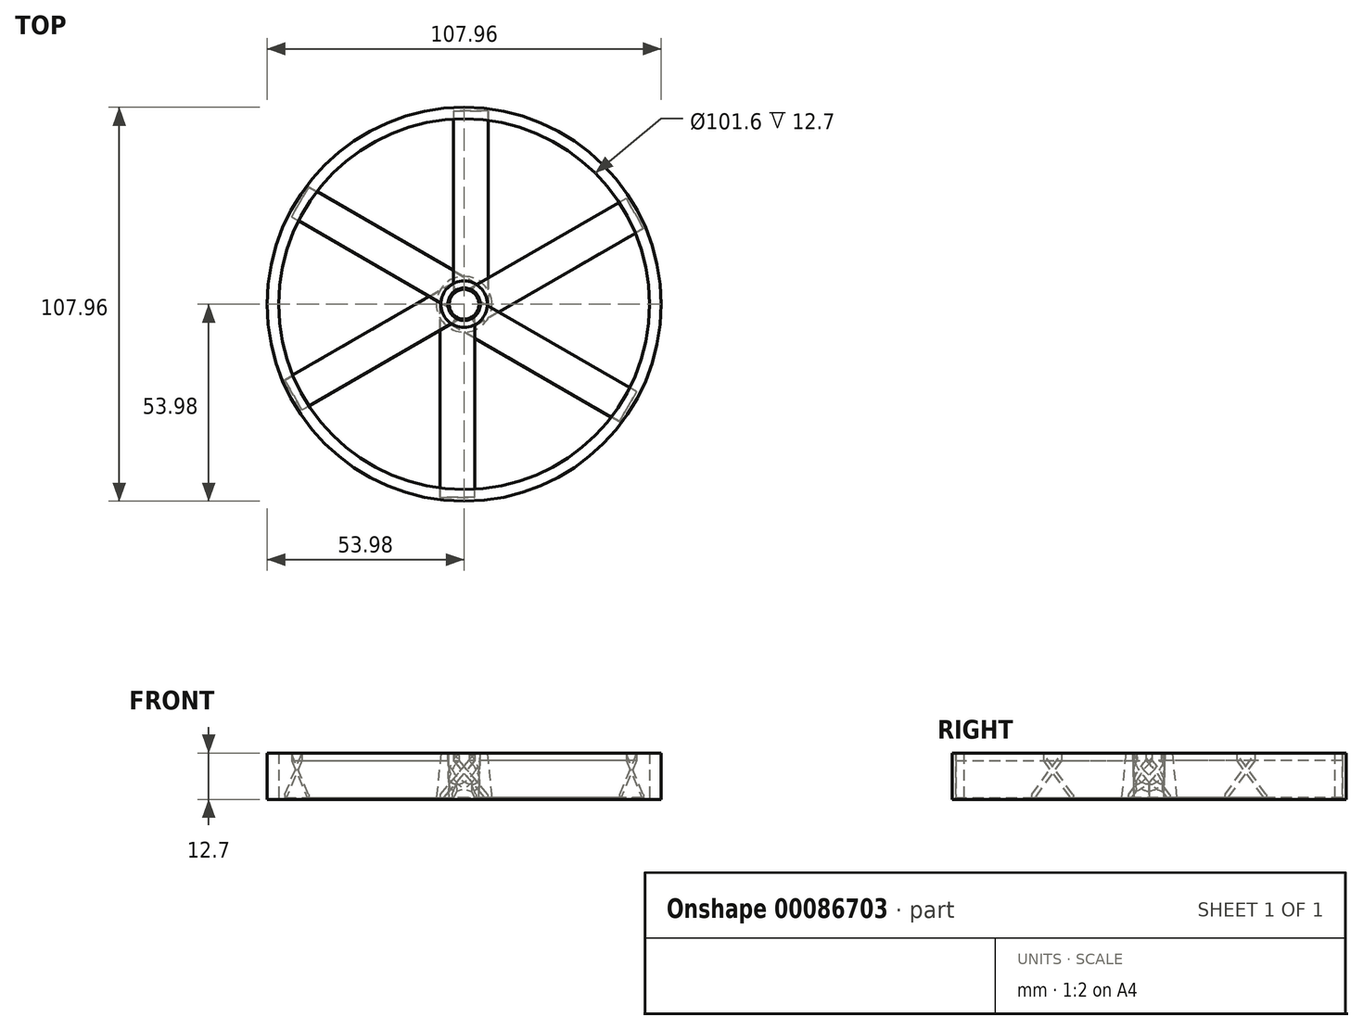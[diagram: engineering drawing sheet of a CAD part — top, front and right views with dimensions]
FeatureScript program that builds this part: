
annotation { "Feature Type Name" : "Feature", "Feature Type Description" : "" }
export const myFeature = defineFeature(function(context is Context, id is Id, definition is map)
    precondition{}
    {
        {
            var Q0;
            Q0=qCreatedBy(makeId("Top.planeOp"),FACE);
            var sketch = newSketch(context, id + "F0", { "sketchPlane" : qUnion([Q0])});
            skCircle(sketch, "E0", {"center": v(0, 0) * mm, "radius": 7.62 * mm});
            skSolve(sketch);
        }
        {
            var Q0;
            Q0=qCreatedBy(makeId("Top.planeOp"),FACE);
            cPlane(context, id + "F1", {"entities" : qUnion([Q0]), "cplaneType" : CPlaneType.OFFSET, "offset" : 12.7 * mm, "width" : 152.4 * mm, "height" : 152.4 * mm});
        }
        {
            var Q0;
            Q0=qCreatedBy(id+"F1.planeOp",FACE);
            var sketch = newSketch(context, id + "F2", { "sketchPlane" : qUnion([Q0])});
            skCircle(sketch, "E1", {"center": v(0, 0) * mm, "radius": 6.35 * mm});
            skSolve(sketch);
        }
        {
            var Q0;
            Q0=makeQuery(id+"F0.imprint","IMPRINT",FACE,{"disambiguationData":[TD([[makeQuery(id+"F0.imprint","IMPRINT",EDGE,{"derivedFrom":sQuery(id+"F0.wireOp",EDGE,"E0")}),1.0]])]});
            var Q1;
            Q1=makeQuery(id+"F2.imprint","IMPRINT",FACE,{"disambiguationData":[TD([[makeQuery(id+"F2.imprint","IMPRINT",EDGE,{"derivedFrom":sQuery(id+"F2.wireOp",EDGE,"E1")}),1.0]])]});
            loft(context, id + "F3", {"sheetProfilesArray" : [{ "sheetProfileEntities" : qUnion([Q0]) }, { "sheetProfileEntities" : qUnion([Q1]) }]});
        }
        {
            var Q0;
            Q0=qCreatedBy(makeId("Top.planeOp"),FACE);
            var sketch = newSketch(context, id + "F4", { "sketchPlane" : qUnion([Q0])});
            skCircle(sketch, "E2", {"center": v(0, 0) * mm, "radius": 4.06 * mm});
            skSolve(sketch);
        }
        {
            var Q0;
            Q0=qCreatedBy(id+"F1.planeOp",FACE);
            var sketch = newSketch(context, id + "F5", { "sketchPlane" : qUnion([Q0])});
            skCircle(sketch, "E3", {"center": v(0, 0) * mm, "radius": 4.45 * mm});
            skSolve(sketch);
        }
        {
            var Q0;
            Q0=qCreatedBy(makeId("Top.planeOp"),FACE);
            var sketch = newSketch(context, id + "F6", { "sketchPlane" : qUnion([Q0])});
            skCircle(sketch, "E4", {"center": v(0, 0) * mm, "radius": 50.8 * mm});
            skCircle(sketch, "E5", {"center": v(0, 0) * mm, "radius": 53.98 * mm});
            skSolve(sketch);
        }
        {
            var Q0;
            Q0 = qSketchRegion(id + "F6", true);
            extrude(context, id + "F7", {"entities" : qUnion([Q0]), "depth" : 12.7 * mm});
        }
        {
            var Q0;
            Q0=qCreatedBy(makeId("Front.planeOp"),FACE);
            var sketch = newSketch(context, id + "F8", { "sketchPlane" : qUnion([Q0])});
            skLineSegment(sketch, "E6", {"start": v(-6.01, 0) * mm, "end": v(-6.95, 0.79) * mm});
            skLineSegment(sketch, "E7", {"start": v(-6.95, 0.79) * mm, "end": v(2.9, 12.52) * mm});
            skLineSegment(sketch, "E8", {"start": v(2.9, 12.52) * mm, "end": v(2.9, 10.6) * mm});
            skLineSegment(sketch, "E9", {"start": v(2.9, 10.6) * mm, "end": v(-6.01, 0) * mm});
            skSolve(sketch);
        }
        {
            var Q0;
            Q0 = qSketchRegion(id + "F8", true);
            extrude(context, id + "F9", {"entities" : qUnion([Q0]), "depth" : 52.95 * mm});
        }
        {
            var Q0;
            Q0=makeQuery(id+"F9.opExtrude","SWEPT_EDGE",EDGE,{"disambiguationData":[OSD([sQuery(id+"F8.wireOp",EDGE,"E6"),sQuery(id+"F8.wireOp",EDGE,"E7")])]});
            var Q1;
            Q1=makeQuery(id+"F9.opExtrude","SWEPT_EDGE",EDGE,{"disambiguationData":[OSD([sQuery(id+"F8.wireOp",EDGE,"E6"),sQuery(id+"F8.wireOp",EDGE,"E9")])]});
            fillet(context, id + "F10", {"entities" : qUnion([Q0, Q1]), "radius" : 0.76 * mm, "tangentPropagation" : true, "allowEdgeOverflow" : false});
        }
        {
            var Q0;
            Q0=qCreatedBy(makeId("Front.planeOp"),FACE);
            var sketch = newSketch(context, id + "F11", { "sketchPlane" : qUnion([Q0])});
            skLineSegment(sketch, "E10", {"start": v(0, 0) * mm, "end": v(0, 37.18) * mm, "construction": true});
            skSolve(sketch);
        }
        {
            var Q0;
            Q0=makeQuery(id+"F9.opExtrude","SWEPT_BODY",BODY,{"disambiguationData":[OSD([sQuery(id+"F8.wireOp",EDGE,"E6"),sQuery(id+"F8.wireOp",EDGE,"E7"),sQuery(id+"F8.wireOp",EDGE,"E8"),sQuery(id+"F8.wireOp",EDGE,"E9")])]});
            var Q1;
            Q1=sQuery(id+"F11.wireOp",EDGE,"E10");
            circularPattern(context, id + "F12", {"entities" : qUnion([Q0]), "axis" : qUnion([Q1]), "angle" : 360 * degree, "instanceCount" : 6, "equalSpace" : true});
        }
        {
            var Q1;
            Q1=makeQuery(id+"F4.imprint","IMPRINT",FACE,{"disambiguationData":[TD([[makeQuery(id+"F4.imprint","IMPRINT",EDGE,{"derivedFrom":sQuery(id+"F4.wireOp",EDGE,"E2")}),1.0]])]});
            var Q2;
            Q2=makeQuery(id+"F5.imprint","IMPRINT",FACE,{"disambiguationData":[TD([[makeQuery(id+"F5.imprint","IMPRINT",EDGE,{"derivedFrom":sQuery(id+"F5.wireOp",EDGE,"E3")}),1.0]])]});
            loft(context, id + "F13", {"operationType" : NewBodyOperationType.REMOVE, "sheetProfilesArray" : [{ "sheetProfileEntities" : qUnion([Q1]) }, { "sheetProfileEntities" : qUnion([Q2]) }]});
        }
    });
